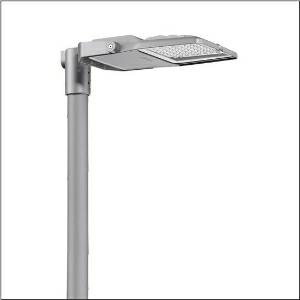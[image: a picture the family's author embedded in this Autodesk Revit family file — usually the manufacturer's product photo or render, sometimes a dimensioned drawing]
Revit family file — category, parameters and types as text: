
# Revit family: floodlight_fl_21_iq_mini___pl43_5xa7772b2a3a_a256
name_source: partatom
category: Lighting Fixtures
units: mm (PartAtom-declared; Revit-internal decimal feet)

## family parameters
Cut with Voids When Loaded = No
Host = Face
Light Source = No
Part Type = Normal
Room Calculation Point = No
Round Connector Dimension = Use Diameter
Shared = No

## types (1)
- --- (1 x LED, 6400 lm, 45.5 W, 3000K)
    Apparent Load = 46 VA
    CIE Flux Codes = 27 78 99 100 100
    Color Rendering = 70
    Color Temperature = 3000K
    Default Elevation = 1800 mm
    Description = Floodlight FL 21 iQ mini, floodlight, primary light control with lens, of PMMA, primary optical cover: protective disc, of toughened safety glass, transparent, light distribution: PL43, light emission: direct distribution, installation type: surface-mounted, lamps: LED, High Power LED, rated values: 6.400lm | 45,5W | 140,7lm/W (begin service life); end service life: 6.400lm | 48W; at 50% lumin. flux: 3.200lm | 21,5W | 148,8lm/W, colour temperature: 3000K, colour rendering: CRI > 70, light colour: 730, light setting 1 begin service life: 100% | 6.400lm | 45,5W | 140,7lm/W | 3.000K, light setting 1 end service life: 48W, further light settings possible, control: pre-setting: linear dimming characteristic, Auto-Match, Temp-Guard, Night-Set, Smart-Wire, Desk-Remote (wireless, voltage-free reading and setting of iQ features in the workshop via application-optimized NFC function/RFID function), optimised constant luminous flux control (CLO 2.0), Light-Fading, Lumen-Switch, with terminal, 6-pole, mains connection: 220..240V, AC, 50/60Hz, luminaire housing, of diecast aluminium, powder-coated, SITECO metallic grey (DB 702S), corrosivity category C5 mid according to DIN EN ISO 12944suitable for swimming poolschlorine-resistant, sealing non-destructively replaceable, please order mast flange separately, mast bracket, of steel, galvanised, powder-coated, protection rating (complete): IP66, insulation class (complete): insulation class II (safety insulation), certification: CE, ENEC, VDE, protection symbol: D, impact resistance: IK08, permissible operating ambient temperature: -40..+40°C, permissible operating ambient temperature for outdoor applications: -40..+50°C, standard: DIN EN 12944, LABS conformity tested according to VDMA 24364:2018-05, packaging unit: 1 piece

Light Distribution: PL43
    Height = 70 mm
    Lamp = 1 x LED
    Lamp Light Flux = 6400 lm
    Lamp Power = 45.5 W
    Lamp count = 1
    Length = 485 mm
    Luminous efficacy = 141 lm/W
    Manufacturer = Siteco
    ModVariant = No
    Model = 5XA7772B2A3A
    Number of Poles = 1
    OnlyDefault = Yes
    Power Factor = 1
    Product Name = Floodlight FL 21 iQ mini | PL43
    Product group = floodlight | pylon annexe
    ProductGroupID = 6201
    Protection Class = Protection class II
    Protection Degree = IP 66
    RLX_Detail_Level = 1
    RLX_Emergency_Light_Flux = 0 lm
    RLX_Emergency_Type = 0
    RLX_Emergency_Type_DB = No
    RlxData = <blob elided: 101285 chars, md5=f93d124a>
    Socket = socket
    Standby Power = 0 W
    System Light Flux = 6400 lm
    System Power = 46 W
    Type Comments = factory setting: luminous flux: 100 % | dim-lin: 254 | 463 mA
    Type Image = l_1007125.jpg
    URL = http://relux.com
    VarID = @adj_162251
    Voltage = 0 V
    Weight = 0.00 kg
    Width = 337 mm

## geometry (parser evidence)
native form markers: Blend x4, Sweep x14
no freeform markers — native parametric forms only
